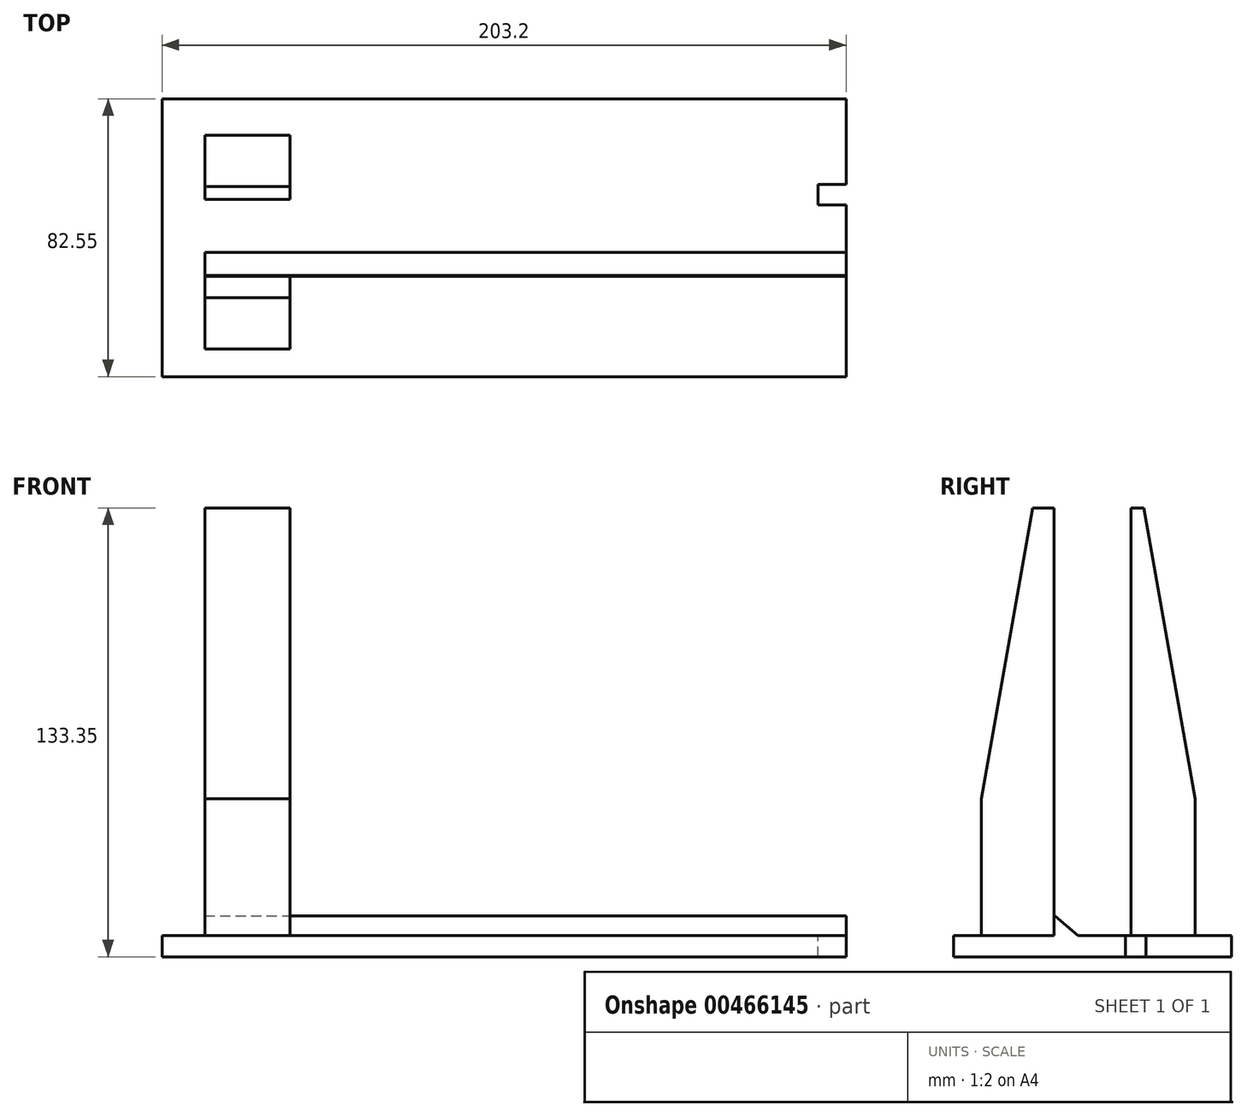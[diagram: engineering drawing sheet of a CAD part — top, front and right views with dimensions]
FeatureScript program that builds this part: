
annotation { "Feature Type Name" : "Feature", "Feature Type Description" : "" }
export const myFeature = defineFeature(function(context is Context, id is Id, definition is map)
    precondition{}
    {
        {
            var Q0;
            Q0=qCreatedBy(makeId("Top.planeOp"),FACE);
            var sketch = newSketch(context, id + "F0", { "sketchPlane" : qUnion([Q0])});
            skLineSegment(sketch, "E0.bottom", {"start": v(-63.59, -51.72) * mm, "end": v(139.61, -51.72) * mm});
            skLineSegment(sketch, "E0.top", {"start": v(-63.59, -134.27) * mm, "end": v(139.61, -134.27) * mm});
            skLineSegment(sketch, "E0.left", {"start": v(-63.59, -51.72) * mm, "end": v(-63.59, -134.27) * mm});
            skLineSegment(sketch, "E0.right", {"start": v(139.61, -51.72) * mm, "end": v(139.61, -134.27) * mm});
            skSolve(sketch);
        }
        {
            var Q0;
            Q0 = qSketchRegion(id + "F0", true);
            extrude(context, id + "F1", {"entities" : qUnion([Q0]), "depth" : 6.35 * mm});
        }
        {
            var Q0;
            Q0=makeQuery(id+"F1.opExtrude","CAP_FACE",FACE,{"disambiguationData":[OSD([sQuery(id+"F0.wireOp",EDGE,"E0.bottom"),sQuery(id+"F0.wireOp",EDGE,"E0.top"),sQuery(id+"F0.wireOp",EDGE,"E0.left"),sQuery(id+"F0.wireOp",EDGE,"E0.right")])],"isStart":false});
            var sketch = newSketch(context, id + "F2", { "sketchPlane" : qUnion([Q0])});
            skLineSegment(sketch, "E1.bottom", {"start": v(139.61, -77.12) * mm, "end": v(125.64, -77.12) * mm});
            skLineSegment(sketch, "E1.top", {"start": v(139.61, -108.87) * mm, "end": v(125.64, -108.87) * mm});
            skLineSegment(sketch, "E1.left", {"start": v(139.61, -77.12) * mm, "end": v(139.61, -108.87) * mm});
            skLineSegment(sketch, "E1.right", {"start": v(125.64, -77.12) * mm, "end": v(125.64, -108.87) * mm});
            skLineSegment(sketch, "E2.bottom", {"start": v(139.61, -77.12) * mm, "end": v(131.23, -77.12) * mm});
            skLineSegment(sketch, "E2.top", {"start": v(139.61, -83.22) * mm, "end": v(131.23, -83.22) * mm});
            skLineSegment(sketch, "E2.left", {"start": v(139.61, -77.12) * mm, "end": v(139.61, -83.22) * mm});
            skLineSegment(sketch, "E2.right", {"start": v(131.23, -77.12) * mm, "end": v(131.23, -83.22) * mm});
            skLineSegment(sketch, "E3.bottom", {"start": v(139.61, -108.87) * mm, "end": v(131.23, -108.87) * mm});
            skLineSegment(sketch, "E3.top", {"start": v(139.61, -102.77) * mm, "end": v(131.23, -102.77) * mm});
            skLineSegment(sketch, "E3.left", {"start": v(139.61, -108.87) * mm, "end": v(139.61, -102.77) * mm});
            skLineSegment(sketch, "E3.right", {"start": v(131.23, -108.87) * mm, "end": v(131.23, -102.77) * mm});
            skSolve(sketch);
        }
        {
            var Q0;
            Q0=makeQuery(id+"F2.imprint","IMPRINT",FACE,{"disambiguationData":[TD([[makeQuery(id+"F2.imprint","IMPRINT",EDGE,{"derivedFrom":sQuery(id+"F2.wireOp",EDGE,"E1.bottom")}),1.0]])]});
            extrude(context, id + "F3", {"entities" : qUnion([Q0]), "operationType" : NewBodyOperationType.REMOVE, "oppositeDirection" : true, "depth" : 25.4 * mm});
        }
        {
            var Q0;
            Q0=makeQuery(id+"F1.opExtrude","CAP_FACE",FACE,{"disambiguationData":[OSD([sQuery(id+"F0.wireOp",EDGE,"E0.bottom"),sQuery(id+"F0.wireOp",EDGE,"E0.top"),sQuery(id+"F0.wireOp",EDGE,"E0.left"),sQuery(id+"F0.wireOp",EDGE,"E0.right")])],"isStart":false});
            var sketch = newSketch(context, id + "F4", { "sketchPlane" : qUnion([Q0])});
            skLineSegment(sketch, "E4.bottom", {"start": v(-50.89, -81.56) * mm, "end": v(-25.49, -81.56) * mm});
            skLineSegment(sketch, "E4.top", {"start": v(-50.89, -104.42) * mm, "end": v(-25.49, -104.42) * mm});
            skLineSegment(sketch, "E4.left", {"start": v(-50.89, -81.56) * mm, "end": v(-50.89, -104.42) * mm});
            skLineSegment(sketch, "E4.right", {"start": v(-25.49, -81.56) * mm, "end": v(-25.49, -104.42) * mm});
            skLineSegment(sketch, "E5.top", {"start": v(-50.89, -62.51) * mm, "end": v(-25.49, -62.51) * mm});
            skLineSegment(sketch, "E5.left", {"start": v(-50.89, -81.56) * mm, "end": v(-50.89, -62.51) * mm});
            skLineSegment(sketch, "E5.right", {"start": v(-25.49, -81.56) * mm, "end": v(-25.49, -62.51) * mm});
            skLineSegment(sketch, "E6.top", {"start": v(-50.89, -126.01) * mm, "end": v(-25.49, -126.01) * mm});
            skLineSegment(sketch, "E6.left", {"start": v(-50.89, -104.42) * mm, "end": v(-50.89, -126.01) * mm});
            skLineSegment(sketch, "E6.right", {"start": v(-25.49, -104.42) * mm, "end": v(-25.49, -126.01) * mm});
            skLineSegment(sketch, "E7.bottom", {"start": v(-63.59, -81.56) * mm, "end": v(139.61, -81.56) * mm});
            skLineSegment(sketch, "E7.top", {"start": v(-63.59, -97.31) * mm, "end": v(139.61, -97.31) * mm});
            skLineSegment(sketch, "E7.left", {"start": v(-63.59, -81.56) * mm, "end": v(-63.59, -97.31) * mm});
            skLineSegment(sketch, "E7.right", {"start": v(139.61, -81.56) * mm, "end": v(139.61, -97.31) * mm});
            skLineSegment(sketch, "E8.top", {"start": v(-63.59, -104.42) * mm, "end": v(139.61, -104.42) * mm});
            skLineSegment(sketch, "E8.left", {"start": v(-63.59, -97.31) * mm, "end": v(-63.59, -104.42) * mm});
            skLineSegment(sketch, "E8.right", {"start": v(139.61, -97.31) * mm, "end": v(139.61, -104.42) * mm});
            skSolve(sketch);
        }
        {
            var Q0;
            Q0=makeQuery(id+"F4.imprint","IMPRINT",FACE,{"disambiguationData":[TD([[makeQuery(id+"F4.imprint","IMPRINT",EDGE,{"derivedFrom":sQuery(id+"F4.wireOp",EDGE,"E6.top")}),1.0]])]});
            var Q1;
            Q1=makeQuery(id+"F4.imprint","IMPRINT",FACE,{"disambiguationData":[TD([[makeQuery(id+"F4.imprint","IMPRINT",EDGE,{"derivedFrom":sQuery(id+"F4.wireOp",EDGE,"E5.top")}),-1.0]])]});
            var Q2;
            Q2=makeQuery(id+"FHYM1uovf032cOH_2.imprint","IMPRINT",FACE,{"disambiguationData":[TD([[makeQuery(id+"FHYM1uovf032cOH_2.imprint","IMPRINT",EDGE,{"derivedFrom":sQuery(id+"FHYM1uovf032cOH_2.wireOp",EDGE,"c0515243-966b-4f10-b740-dc8fe948e2ae.top")}),1.0]])]});
            var Q3;
            Q3=makeQuery(id+"FHYM1uovf032cOH_2.imprint","IMPRINT",FACE,{"disambiguationData":[TD([[makeQuery(id+"FHYM1uovf032cOH_2.imprint","IMPRINT",EDGE,{"derivedFrom":sQuery(id+"FHYM1uovf032cOH_2.wireOp",EDGE,"a2d4cf59-e919-49b2-a9bb-9520842440b4.top")}),-1.0]])]});
            extrude(context, id + "F5", {"entities" : qUnion([Q0, Q1, Q2, Q3]), "depth" : 127 * mm});
        }
        {
            var Q0;
            Q0=makeQuery(id+"F5.opExtrude","CAP_EDGE",EDGE,{"disambiguationData":[OSD([sQuery(id+"F4.wireOp",EDGE,"E6.top")])],"isStart":false});
            var Q1;
            Q1=makeQuery(id+"F5.opExtrude","CAP_EDGE",EDGE,{"disambiguationData":[OSD([sQuery(id+"FHYM1uovf032cOH_2.wireOp",EDGE,"c0515243-966b-4f10-b740-dc8fe948e2ae.top")])],"isStart":false});
            chamfer(context, id + "F6", {"entities" : qUnion([Q0, Q1]), "chamferType" : ChamferType.OFFSET_ANGLE, "width" : 15.24 * mm, "oppositeDirection" : false, "angle" : 80 * degree, "tangentPropagation" : true});
        }
        {
            var Q0;
            Q0=makeQuery(id+"F5.opExtrude","CAP_EDGE",EDGE,{"disambiguationData":[OSD([sQuery(id+"F4.wireOp",EDGE,"E5.top")])],"isStart":false});
            var Q1;
            Q1=makeQuery(id+"F5.opExtrude","CAP_EDGE",EDGE,{"disambiguationData":[OSD([sQuery(id+"FHYM1uovf032cOH_2.wireOp",EDGE,"a2d4cf59-e919-49b2-a9bb-9520842440b4.top")])],"isStart":false});
            chamfer(context, id + "F7", {"entities" : qUnion([Q0, Q1]), "chamferType" : ChamferType.OFFSET_ANGLE, "width" : 15.24 * mm, "oppositeDirection" : true, "angle" : 80 * degree, "tangentPropagation" : true});
        }
        {
            var Q0;
            {var subQ1=sQuery(id+"F4.wireOp",EDGE,"E4.right");var subQ3=sQuery(id+"F4.wireOp",EDGE,"E7.top");var subQ4=makeQuery(id+"F4.imprint","INTERSECT",VERTEX,{"derivedFrom":[subQ1,subQ3]});Q0=makeQuery(id+"F4.imprint","IMPRINT",FACE,{"disambiguationData":[TD([[makeQuery(id+"F4.imprint","IMPRINT",EDGE,{"disambiguationData":[TD([[subQ4,-1.0]])],"derivedFrom":subQ3}),-1.0]])]});}
            var Q1;
            {var subQ1=sQuery(id+"F4.wireOp",EDGE,"E4.left");var subQ3=sQuery(id+"F4.wireOp",EDGE,"E7.top");var subQ4=makeQuery(id+"F4.imprint","INTERSECT",VERTEX,{"derivedFrom":[subQ1,subQ3]});Q1=makeQuery(id+"F4.imprint","IMPRINT",FACE,{"disambiguationData":[TD([[makeQuery(id+"F4.imprint","IMPRINT",EDGE,{"disambiguationData":[TD([[subQ4,-1.0]])],"derivedFrom":subQ3}),-1.0]])]});}
            var Q2;
            {var subQ1=sQuery(id+"FHYM1uovf032cOH_2.wireOp",EDGE,"98914256-8aca-4dfa-bfae-99a6503d454c.left");var subQ3=sQuery(id+"FHYM1uovf032cOH_2.wireOp",EDGE,"odhto8og-kZTI-aVGY-iGIe-T9WPoUQdVJ1u.bottom");var subQ4=makeQuery(id+"FHYM1uovf032cOH_2.imprint","INTERSECT",VERTEX,{"derivedFrom":[subQ1,subQ3]});Q2=makeQuery(id+"FHYM1uovf032cOH_2.imprint","IMPRINT",FACE,{"disambiguationData":[TD([[makeQuery(id+"FHYM1uovf032cOH_2.imprint","IMPRINT",EDGE,{"disambiguationData":[TD([[subQ4,1.0]])],"derivedFrom":subQ3}),1.0]])]});}
            var Q3;
            {var subQ5=sQuery(id+"FHYM1uovf032cOH_2.wireOp",EDGE,"odhto8og-kZTI-aVGY-iGIe-T9WPoUQdVJ1u.bottom");var subQ7=sQuery(id+"FHYM1uovf032cOH_2.wireOp",EDGE,"98914256-8aca-4dfa-bfae-99a6503d454c.left");var subQ9=makeQuery(id+"FHYM1uovf032cOH_2.imprint","INTERSECT",VERTEX,{"derivedFrom":[subQ7,subQ5]});Q3=makeQuery(id+"FHYM1uovf032cOH_2.imprint","IMPRINT",FACE,{"disambiguationData":[TD([[makeQuery(id+"FHYM1uovf032cOH_2.imprint","IMPRINT",EDGE,{"disambiguationData":[TD([[subQ9,-1.0]])],"derivedFrom":subQ7}),-1.0]])]});}
            extrude(context, id + "F8", {"entities" : qUnion([Q0, Q1, Q2, Q3]), "operationType" : NewBodyOperationType.ADD, "depth" : 5.84 * mm});
        }
        {
            var Q0;
            Q0=makeQuery(id+"F8.opExtrude","CAP_EDGE",EDGE,{"disambiguationData":[OSD([sQuery(id+"F4.wireOp",EDGE,"E7.top")])],"isStart":false});
            chamfer(context, id + "F9", {"entities" : qUnion([Q0]), "chamferType" : ChamferType.OFFSET_ANGLE, "width" : 5.84 * mm, "oppositeDirection" : false, "angle" : 50 * degree, "tangentPropagation" : true});
        }
    });
